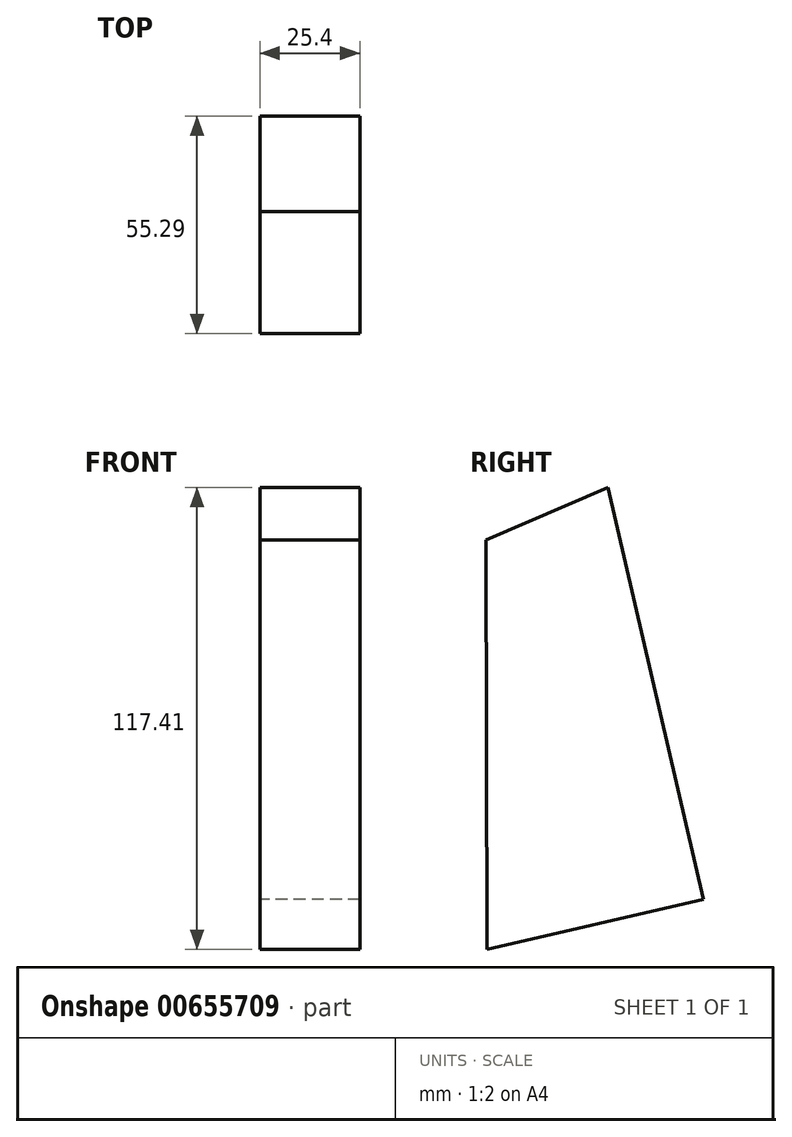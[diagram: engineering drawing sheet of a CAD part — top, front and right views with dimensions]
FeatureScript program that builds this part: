
annotation { "Feature Type Name" : "Feature", "Feature Type Description" : "" }
export const myFeature = defineFeature(function(context is Context, id is Id, definition is map)
    precondition{}
    {
        {
            var Q0;
            Q0=qCreatedBy(makeId("Right.planeOp"),FACE);
            var sketch = newSketch(context, id + "F0", { "sketchPlane" : qUnion([Q0])});
            skLineSegment(sketch, "E0", {"start": v(-100.42, 16.75) * mm, "end": v(-69.36, 30.1) * mm});
            skLineSegment(sketch, "E1", {"start": v(-69.36, 30.1) * mm, "end": v(-45.13, -74.56) * mm});
            skLineSegment(sketch, "E2", {"start": v(-45.13, -74.56) * mm, "end": v(-100.2, -87.3) * mm});
            skLineSegment(sketch, "E3", {"start": v(-100.2, -87.3) * mm, "end": v(-100.2, -87.3) * mm});
            skLineSegment(sketch, "E4", {"start": v(-100.2, -87.3) * mm, "end": v(-100.42, 16.75) * mm});
            skSolve(sketch);
        }
        {
            var Q0;
            Q0 = qSketchRegion(id + "F0", true);
            var Q1;
            Q1=makeQuery(id+"F0.imprint","IMPRINT",FACE,{"disambiguationData":[TD([[makeQuery(id+"F0.imprint","IMPRINT",EDGE,{"derivedFrom":sQuery(id+"F0.wireOp",EDGE,"E0")}),-1.0]])]});
            extrude(context, id + "F1", {"entities" : qUnion([Q0, Q1]), "depth" : 25.4 * mm, "offsetDistance" : 25.4 * mm});
        }
    });
